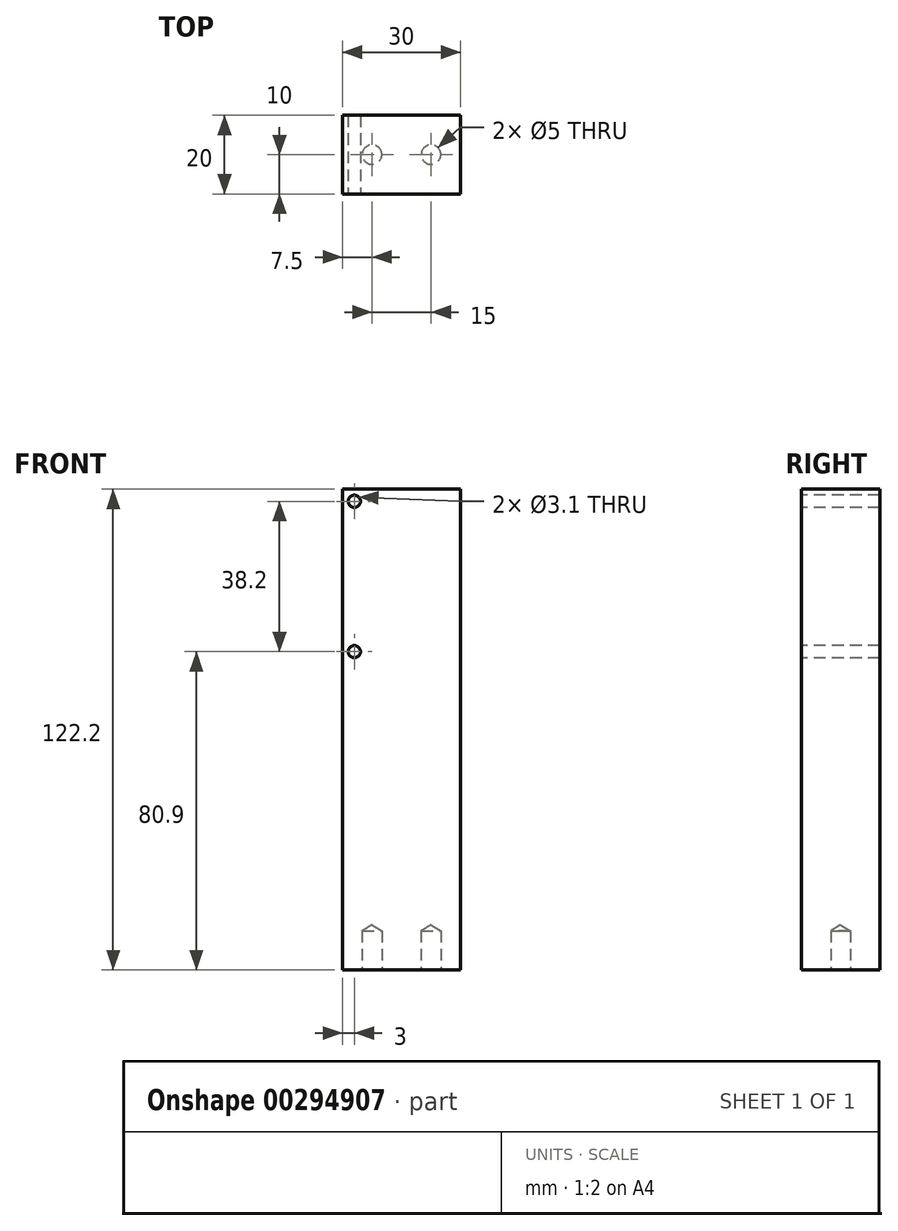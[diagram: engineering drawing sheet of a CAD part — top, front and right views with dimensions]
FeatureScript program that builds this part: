
annotation { "Feature Type Name" : "Feature", "Feature Type Description" : "" }
export const myFeature = defineFeature(function(context is Context, id is Id, definition is map)
    precondition{}
    {
        {
            var Q0;
            Q0=qCreatedBy(makeId("Front.planeOp"),FACE);
            var sketch = newSketch(context, id + "F0", { "sketchPlane" : qUnion([Q0])});
            skLineSegment(sketch, "E0.bottom", {"start": v(15, 61.1) * mm, "end": v(-15, 61.1) * mm});
            skLineSegment(sketch, "E0.top", {"start": v(15, -61.1) * mm, "end": v(-15, -61.1) * mm});
            skLineSegment(sketch, "E0.left", {"start": v(15, 61.1) * mm, "end": v(15, -61.1) * mm});
            skLineSegment(sketch, "E0.right", {"start": v(-15, 61.1) * mm, "end": v(-15, -61.1) * mm});
            skPoint(sketch, "E0.middle", {"position": v(0, 0) * mm});
            skSolve(sketch);
        }
        {
            var Q0;
            Q0=makeQuery(id+"F0.imprint","IMPRINT",FACE,{"disambiguationData":[TD([[makeQuery(id+"F0.imprint","IMPRINT",EDGE,{"derivedFrom":sQuery(id+"F0.wireOp",EDGE,"E0.bottom")}),1.0]])]});
            extrude(context, id + "F1", {"entities" : qUnion([Q0]), "depth" : 20 * mm});
        }
        {
            var Q0;
            Q0=makeQuery(id+"F1.opExtrude","CAP_FACE",FACE,{"disambiguationData":[OSD([sQuery(id+"F0.wireOp",EDGE,"E0.bottom"),sQuery(id+"F0.wireOp",EDGE,"E0.top"),sQuery(id+"F0.wireOp",EDGE,"E0.left"),sQuery(id+"F0.wireOp",EDGE,"E0.right")])],"isStart":false});
            var sketch = newSketch(context, id + "F2", { "sketchPlane" : qUnion([Q0])});
            skLineSegment(sketch, "E1", {"start": v(-12, 61.1) * mm, "end": v(-12, -61.1) * mm, "construction": true});
            skPoint(sketch, "E2", {"position": v(-12, 58) * mm});
            skPoint(sketch, "E3", {"position": v(-12, 19.8) * mm});
            skSolve(sketch);
        }
        {
            var Q0;
            Q0=sQuery(id+"F2.wireOp",VERTEX,"E2");
            var Q1;
            Q1=sQuery(id+"F2.wireOp",VERTEX,"E3");
            var Q2;
            Q2=makeQuery(id+"F1.opExtrude","SWEPT_BODY",BODY,{"disambiguationData":[OSD([sQuery(id+"F0.wireOp",EDGE,"E0.bottom"),sQuery(id+"F0.wireOp",EDGE,"E0.top"),sQuery(id+"F0.wireOp",EDGE,"E0.left"),sQuery(id+"F0.wireOp",EDGE,"E0.right")])]});
            hole(context, id + "F3", {"style" : HoleStyle.SIMPLE, "endStyle" : HoleEndStyle.THROUGH, "holeDiameter" : 3.1 * mm, "tappedDepth" : 12 * mm, "tapClearance" : 3, "locations" : qUnion([Q0, Q1]), "scope" : qUnion([Q2])});
        }
        {
            var Q0;
            Q0=makeQuery(id+"F1.opExtrude","SWEPT_FACE",FACE,{"disambiguationData":[OSD([sQuery(id+"F0.wireOp",EDGE,"E0.top")])]});
            var sketch = newSketch(context, id + "F4", { "sketchPlane" : qUnion([Q0])});
            skLineSegment(sketch, "E4", {"start": v(-15, 10) * mm, "end": v(15, 10) * mm, "construction": true});
            skPoint(sketch, "E5", {"position": v(7.5, 10) * mm});
            skPoint(sketch, "E6", {"position": v(-7.5, 10) * mm});
            skSolve(sketch);
        }
        {
            var Q0;
            Q0=sQuery(id+"F4.wireOp",VERTEX,"E6");
            var Q1;
            Q1=sQuery(id+"F4.wireOp",VERTEX,"E5");
            var Q2;
            Q2=makeQuery(id+"F1.opExtrude","SWEPT_BODY",BODY,{"disambiguationData":[OSD([sQuery(id+"F0.wireOp",EDGE,"E0.bottom"),sQuery(id+"F0.wireOp",EDGE,"E0.top"),sQuery(id+"F0.wireOp",EDGE,"E0.left"),sQuery(id+"F0.wireOp",EDGE,"E0.right")])]});
            hole(context, id + "F5", {"style" : HoleStyle.SIMPLE, "endStyle" : HoleEndStyle.BLIND, "holeDiameter" : 5 * mm, "holeDepth" : 10 * mm, "tappedDepth" : 12 * mm, "tapClearance" : 3, "locations" : qUnion([Q0, Q1]), "scope" : qUnion([Q2])});
        }
    });
